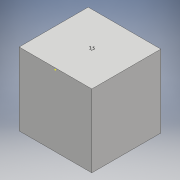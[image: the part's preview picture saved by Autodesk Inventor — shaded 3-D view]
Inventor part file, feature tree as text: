
AUTODESK INVENTOR PART (.ipt)
format: ipt  version: 2017 (Build 210142000, 142)  size: 151,040 bytes
history: native  units: mm
features: sketch x7, extrude x5, hole x1
ambient origin geometry x8: Origin, YZ Plane, XZ Plane, XY Plane, X Axis, Y Axis, Z Axis, Center Point
bodies: Solid1 (feature_tree)
feature tree (13):
  extrude  "Extrusion1"  Depth=100.0mm
  extrude  "Extrusion2"  Depth=95.0mm TaperAngle=0.0deg
  hole  "Hole2"  [1 undecoded]
  extrude  "Extrusion4"  Depth=5.0mm
  extrude  "Extrusion5"  Depth=85.0mm
  extrude  "Extrusion6"  Depth=2.5mm
  sketch  "Sketch13"  dims[d15=2.5mm d16=2.0mm d17=2.5mm d18=2.5mm d19=2.5mm d20=2.5mm d28=2.0mm d29=6.0mm d30=4.0mm d31=2.0mm d32=90.0deg d33=8.0mm d34=0.0mm d66=21.0mm d67=3.0mm d68=0.0mm d69=21.0mm d70=3.0mm d71=0.0mm d72=45.0mm d73=45.0mm d74=21.0mm d75=3.0mm d76=0.0mm d77=3.5mm d11=1.0mm d21=1.0mm d22=1.0mm]
  sketch  "Sketch1"  dims[d0=100.0mm d1=100.0mm]
  sketch  "Sketch2"  dims[d2=50.0mm d3=95.0mm d4=0.0mm]
  sketch  "Sketch3"  dims[d5=5.0mm d6=5.0mm]
  sketch  "Sketch9"  dims[d7=5.0mm d8=5.0mm]
  sketch  "Sketch10"  dims[d9=85.0mm d10=0.0mm d12=2.5mm]
  sketch  "Sketch11"  dims[d13=2.5mm d14=2.5mm]
note: 1 required parameter value undecoded (feature->parameter linkage not recoverable at this tier; creation-order binding heuristic only, values carry confidence <= 0.55)
